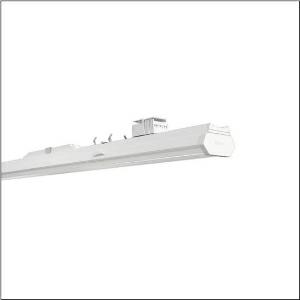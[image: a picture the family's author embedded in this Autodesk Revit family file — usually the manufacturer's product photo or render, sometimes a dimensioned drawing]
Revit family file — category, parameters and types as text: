
# Revit family: licross_r__21_protected_mo_52td12dn68xg_d3b6
name_source: partatom
category: Lighting Fixtures
units: mm (PartAtom-declared; Revit-internal decimal feet)

## family parameters
Cut with Voids When Loaded = No
Host = Face
Light Source = No
Part Type = Normal
Room Calculation Point = No
Round Connector Dimension = Use Diameter
Shared = No

## types (1)
- --- (1 x LED, 8000 lm, 46.6 W, 6500K)
    Apparent Load = 47 VA
    CIE Flux Codes = 73 92 98 99 100
    Color Rendering = 80
    Color Temperature = 6500K
    Default Elevation = 1800 mm
    Description = Licross® 21 Protected MO, luminaire insert, of sheet steel, galvanised, coil coated, white, length: 1.500mm, width: 90mm, height: 103mm, LED rated luminous flux: 8.000lm, light colour: 865, control gear: DALI 2, with plug, 5-pole, with phase selection, mains connection: 220..240V, AC, 50/60Hz, rated input power: 47W, halogen-free wiring, primary light control with lens, of plastic, primary optical cover: cover, of PMMA, light emission: direct distribution, primary light characteristic: symmetric, protection rating (complete): IP54, insulation class (complete): insulation class I (protective earthing), certification: CE, ENEC, VDE, UKCA, protection symbol: D if used in an environment with non-conductive dust loads with corresponding accessories, impact resistance: IK06, permissible ambient temperature for indoor applications: -25..+40°C, corresponds to IFS (International Featured Standards) requirements for safety and quality in the food industry, reducing of maximum allowable ambient temperature of 5°C with ceiling mounting, LABS conformity tested according to VDMA 24364:2018-05, packaging unit: 1 piece
    Height = 92 mm
    Lamp = 1 x LED
    Lamp Light Flux = 8000 lm
    Lamp Power = 46.6 W
    Lamp count = 1
    Length = 1500 mm
    Luminous efficacy = 172 lm/W
    Manufacturer = Siteco
    ModVariant = No
    Model = 52TD12DN68XG
    Mounting Place = Ceiling
    Mounting Type = Pendant
    Number of Poles = 1
    OnlyDefault = Yes
    Power Factor = 1
    Product Name = Licross® 21 Protected MO
    Product group = luminaire insert
    ProductGroupID = 902
    Protection Class = Protection class I
    Protection Degree = IP 54
    RLX_Detail_Level = 1
    RLX_Emergency_Light_Flux = 0 lm
    RLX_Emergency_Type = 0
    RLX_Emergency_Type_DB = No
    RlxData = <blob elided: 24341 chars, md5=3624d583>
    Socket = socket
    Standby Power = 0 W
    System Light Flux = 8000 lm
    System Power = 47 W
    Type Comments = factory setting: luminous flux: 100 % | dim-lin: 254 | 315 mA
    Type Image = l_1256148.jpg
    URL = http://relux.com
    VarID = @adj_022702
    Voltage = 0 V
    Weight = 0.00 kg
    Width = 88 mm

## geometry (parser evidence)
native form markers: Blend x4, Sweep x10
no freeform markers — native parametric forms only
